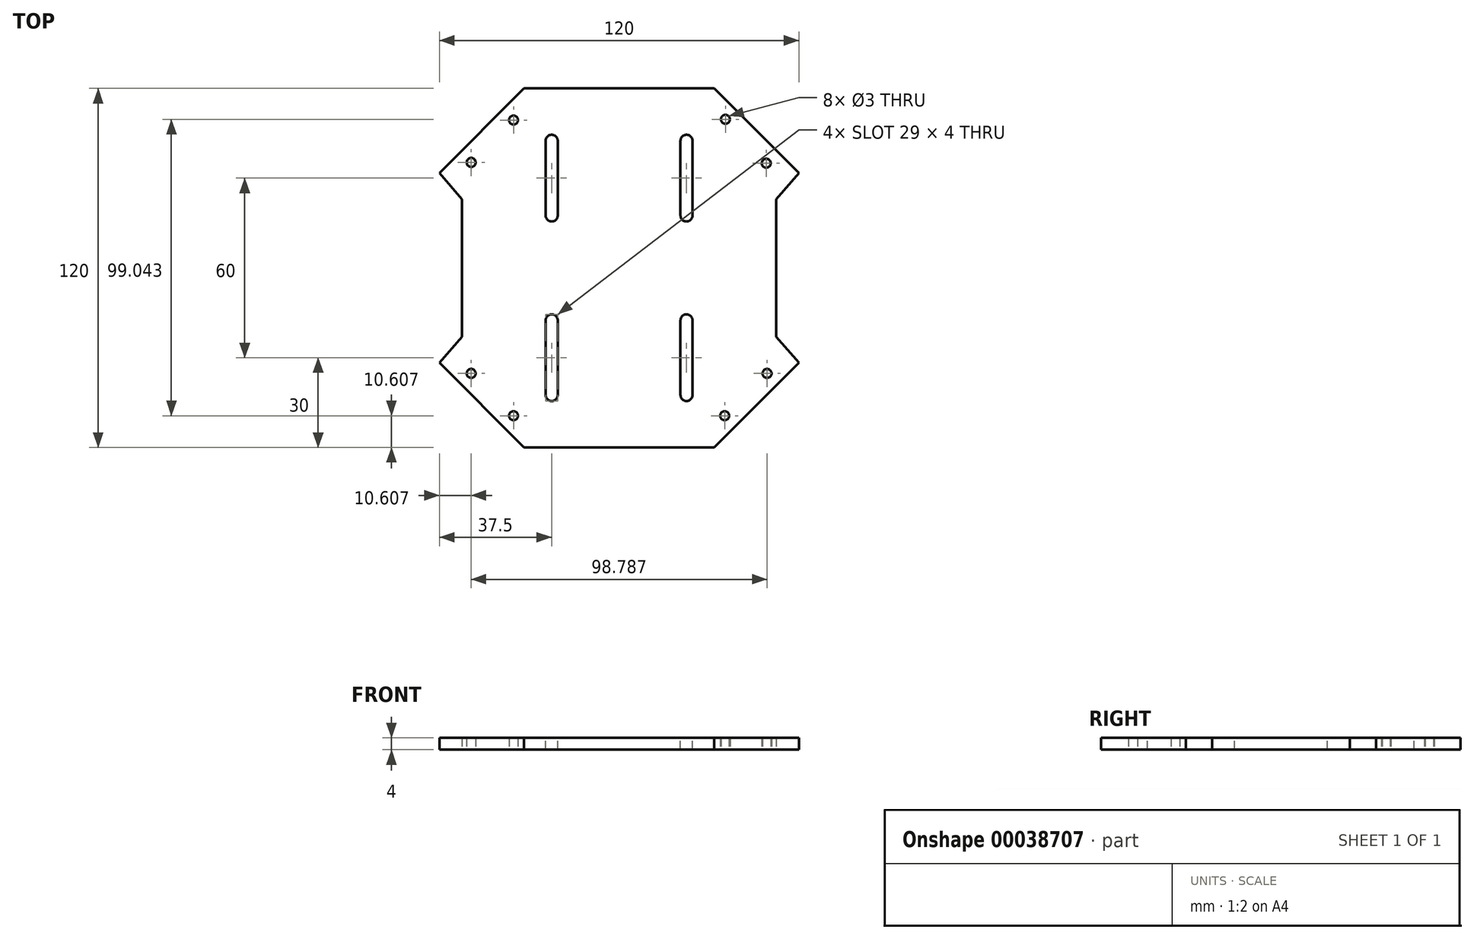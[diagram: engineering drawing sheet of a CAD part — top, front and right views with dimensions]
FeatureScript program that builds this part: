
annotation { "Feature Type Name" : "Feature", "Feature Type Description" : "" }
export const myFeature = defineFeature(function(context is Context, id is Id, definition is map)
    precondition{}
    {
        {
            var Q0;
            Q0=qCreatedBy(makeId("Top.planeOp"),FACE);
            var sketch = newSketch(context, id + "F0", { "sketchPlane" : qUnion([Q0])});
            skLineSegment(sketch, "E0.rect.bottom", {"start": v(32.5, 32.5) * mm, "end": v(-32.5, 32.5) * mm, "construction": true});
            skLineSegment(sketch, "E0.rect.top", {"start": v(32.5, -32.5) * mm, "end": v(-32.5, -32.5) * mm, "construction": true});
            skLineSegment(sketch, "E0.rect.left", {"start": v(32.5, 32.5) * mm, "end": v(32.5, -32.5) * mm, "construction": true});
            skLineSegment(sketch, "E0.rect.right", {"start": v(-32.5, 32.5) * mm, "end": v(-32.5, -32.5) * mm, "construction": true});
            skPoint(sketch, "E0.rect.middle", {"position": v(0, 0) * mm});
            skLineSegment(sketch, "E1", {"start": v(-32.5, -32.5) * mm, "end": v(32.5, 32.5) * mm, "construction": true});
            skLineSegment(sketch, "E2", {"start": v(-32.5, 32.5) * mm, "end": v(32.5, -32.5) * mm, "construction": true});
            skLineSegment(sketch, "E3.bottom", {"start": v(-137.78, 137.78) * mm, "end": v(137.78, 137.78) * mm, "construction": true});
            skLineSegment(sketch, "E3.top", {"start": v(-137.78, -137.78) * mm, "end": v(137.78, -137.78) * mm, "construction": true});
            skLineSegment(sketch, "E3.left", {"start": v(-137.78, 137.78) * mm, "end": v(-137.78, -137.78) * mm, "construction": true});
            skLineSegment(sketch, "E3.right", {"start": v(137.78, 137.78) * mm, "end": v(137.78, -137.78) * mm, "construction": true});
            skCircle(sketch, "E4", {"center": v(-137.78, 137.78) * mm, "radius": 101.5 * mm, "construction": true});
            skCircle(sketch, "E5", {"center": v(137.78, 137.78) * mm, "radius": 101.5 * mm, "construction": true});
            skCircle(sketch, "E6", {"center": v(137.78, -137.78) * mm, "radius": 101.5 * mm, "construction": true});
            skCircle(sketch, "E7", {"center": v(-137.78, -137.78) * mm, "radius": 101.5 * mm, "construction": true});
            skLineSegment(sketch, "E8.rect.bottom", {"start": v(-20.12, 56) * mm, "end": v(20.13, 56) * mm, "construction": true});
            skLineSegment(sketch, "E8.rect.top", {"start": v(-20.13, -56) * mm, "end": v(20.12, -56) * mm, "construction": true});
            skLineSegment(sketch, "E8.rect.left", {"start": v(-20.12, 56) * mm, "end": v(-20.13, -56) * mm, "construction": true});
            skLineSegment(sketch, "E8.rect.right", {"start": v(20.13, 56) * mm, "end": v(20.12, -56) * mm, "construction": true});
            skLineSegment(sketch, "E9.rect.bottom", {"start": v(-45.86, 45.86) * mm, "end": v(45.86, 45.86) * mm, "construction": true});
            skLineSegment(sketch, "E9.rect.top", {"start": v(-45.86, -45.86) * mm, "end": v(45.86, -45.86) * mm, "construction": true});
            skLineSegment(sketch, "E9.rect.left", {"start": v(-45.86, 45.86) * mm, "end": v(-45.86, -45.86) * mm, "construction": true});
            skLineSegment(sketch, "E9.rect.right", {"start": v(45.86, 45.86) * mm, "end": v(45.86, -45.86) * mm, "construction": true});
            skLineSegment(sketch, "E10", {"start": v(45.86, 45.86) * mm, "end": v(137.78, 137.78) * mm, "construction": true});
            skLineSegment(sketch, "E11", {"start": v(45.86, -45.86) * mm, "end": v(137.78, -137.78) * mm, "construction": true});
            skLineSegment(sketch, "E12", {"start": v(0, -137.78) * mm, "end": v(0, 137.78) * mm, "construction": true});
            skLineSegment(sketch, "E13", {"start": v(-137.78, -137.78) * mm, "end": v(-45.86, -45.86) * mm, "construction": true});
            skCircle(sketch, "E14", {"center": v(-137.78, 137.78) * mm, "radius": 14 * mm, "construction": true});
            skCircle(sketch, "E15", {"center": v(-137.78, 137.78) * mm, "radius": 20 * mm});
            skLineSegment(sketch, "E16", {"start": v(-60, 31.72) * mm, "end": v(-60, -31.72) * mm, "construction": true});
            skLineSegment(sketch, "E17", {"start": v(-60, -31.72) * mm, "end": v(-31.72, -60) * mm, "construction": true});
            skLineSegment(sketch, "E18", {"start": v(31.72, -60) * mm, "end": v(60, -31.72) * mm, "construction": true});
            skLineSegment(sketch, "E19", {"start": v(-31.72, -60) * mm, "end": v(31.72, -60) * mm, "construction": true});
            skLineSegment(sketch, "E20", {"start": v(60, -31.72) * mm, "end": v(60, 31.72) * mm, "construction": true});
            skLineSegment(sketch, "E21", {"start": v(31.72, 60) * mm, "end": v(60, 31.72) * mm, "construction": true});
            skLineSegment(sketch, "E22", {"start": v(-31.72, 60) * mm, "end": v(31.72, 60) * mm, "construction": true});
            skLineSegment(sketch, "E23", {"start": v(-151.92, 123.64) * mm, "end": v(-123.64, 151.92) * mm, "construction": true});
            skLineSegment(sketch, "E24", {"start": v(-52.5, 23) * mm, "end": v(-52.5, -23) * mm, "construction": true});
            skLineSegment(sketch, "E25", {"start": v(-52.5, 0) * mm, "end": v(-60, 0) * mm, "construction": true});
            skLineSegment(sketch, "E26", {"start": v(-60, 31.72) * mm, "end": v(-52.5, 23) * mm, "construction": true});
            skLineSegment(sketch, "E27", {"start": v(-60, -31.72) * mm, "end": v(-52.5, -23) * mm, "construction": true});
            skLineSegment(sketch, "E28", {"start": v(52.5, 23) * mm, "end": v(52.5, -23) * mm, "construction": true});
            skLineSegment(sketch, "E29", {"start": v(52.5, 0) * mm, "end": v(60, 0) * mm, "construction": true});
            skLineSegment(sketch, "E30", {"start": v(60, 31.72) * mm, "end": v(52.5, 23) * mm, "construction": true});
            skLineSegment(sketch, "E31", {"start": v(60, -31.72) * mm, "end": v(52.5, -23) * mm, "construction": true});
            skCircle(sketch, "E32", {"center": v(-137.78, -137.78) * mm, "radius": 20 * mm, "construction": true});
            skCircle(sketch, "E33", {"center": v(137.78, -137.78) * mm, "radius": 20 * mm, "construction": true});
            skCircle(sketch, "E34", {"center": v(137.78, 137.78) * mm, "radius": 20 * mm, "construction": true});
            skLineSegment(sketch, "E35", {"start": v(-151.92, -123.64) * mm, "end": v(-123.64, -151.92) * mm, "construction": true});
            skLineSegment(sketch, "E36", {"start": v(123.64, -151.92) * mm, "end": v(151.92, -123.64) * mm, "construction": true});
            skLineSegment(sketch, "E37", {"start": v(151, 122.77) * mm, "end": v(124.57, 152.8) * mm, "construction": true});
            skLineSegment(sketch, "E38", {"start": v(-60, 31.72) * mm, "end": v(-31.72, 60) * mm});
            skLineSegment(sketch, "E39", {"start": v(-45.86, 45.86) * mm, "end": v(-137.78, 137.78) * mm, "construction": true});
            skLineSegment(sketch, "E40", {"start": v(-112.33, 92.53) * mm, "end": v(-92.53, 112.33) * mm, "construction": true});
            skPoint(sketch, "E41", {"position": v(-102.43, 102.43) * mm});
            skLineSegment(sketch, "E42", {"start": v(-151.92, 123.64) * mm, "end": v(-112.33, 92.53) * mm});
            skLineSegment(sketch, "E43", {"start": v(-112.33, 92.53) * mm, "end": v(-60, 31.72) * mm});
            skLineSegment(sketch, "E44", {"start": v(-123.64, 151.92) * mm, "end": v(-92.53, 112.33) * mm});
            skLineSegment(sketch, "E45", {"start": v(-31.72, 60) * mm, "end": v(-92.53, 112.33) * mm});
            skLineSegment(sketch, "E46", {"start": v(-92.53, -112.33) * mm, "end": v(-112.33, -92.53) * mm, "construction": true});
            skPoint(sketch, "E47", {"position": v(-102.43, -102.43) * mm});
            skLineSegment(sketch, "E48", {"start": v(112.33, 92.53) * mm, "end": v(92.53, 112.33) * mm, "construction": true});
            skLineSegment(sketch, "E49", {"start": v(112.33, -92.53) * mm, "end": v(92.53, -112.33) * mm, "construction": true});
            skPoint(sketch, "E50", {"position": v(102.43, 102.43) * mm});
            skPoint(sketch, "E51", {"position": v(102.43, -102.43) * mm});
            skLineSegment(sketch, "E52", {"start": v(124.57, 152.8) * mm, "end": v(92.53, 112.33) * mm, "construction": true});
            skLineSegment(sketch, "E53", {"start": v(31.72, 60) * mm, "end": v(92.53, 112.33) * mm, "construction": true});
            skLineSegment(sketch, "E54", {"start": v(151, 122.77) * mm, "end": v(112.33, 92.53) * mm, "construction": true});
            skLineSegment(sketch, "E55", {"start": v(60, 31.72) * mm, "end": v(112.33, 92.53) * mm, "construction": true});
            skLineSegment(sketch, "E56", {"start": v(151.92, -123.64) * mm, "end": v(112.33, -92.53) * mm, "construction": true});
            skLineSegment(sketch, "E57", {"start": v(112.33, -92.53) * mm, "end": v(60, -31.72) * mm, "construction": true});
            skLineSegment(sketch, "E58", {"start": v(31.72, -60) * mm, "end": v(92.53, -112.33) * mm, "construction": true});
            skLineSegment(sketch, "E59", {"start": v(123.64, -151.92) * mm, "end": v(92.53, -112.33) * mm, "construction": true});
            skLineSegment(sketch, "E60", {"start": v(-123.64, -151.92) * mm, "end": v(-92.53, -112.33) * mm, "construction": true});
            skLineSegment(sketch, "E61", {"start": v(-31.72, -60) * mm, "end": v(-92.53, -112.33) * mm, "construction": true});
            skLineSegment(sketch, "E62", {"start": v(-60, -31.72) * mm, "end": v(-112.33, -92.53) * mm, "construction": true});
            skLineSegment(sketch, "E63", {"start": v(-151.92, -123.64) * mm, "end": v(-112.33, -92.53) * mm, "construction": true});
            skLineSegment(sketch, "E64", {"start": v(-53.46, 24.11) * mm, "end": v(-24.11, 53.46) * mm});
            skLineSegment(sketch, "E65", {"start": v(-24.11, 53.46) * mm, "end": v(-31.72, 60) * mm});
            skLineSegment(sketch, "E66", {"start": v(-53.46, 24.11) * mm, "end": v(-60, 31.72) * mm});
            skSolve(sketch);
        }
        {
            var Q0;
            Q0=qCreatedBy(makeId("Top.planeOp"),FACE);
            var sketch = newSketch(context, id + "F1", { "sketchPlane" : qUnion([Q0])});
            skLineSegment(sketch, "E67.0", {"start": v(-151.92, 123.64) * mm, "end": v(-112.33, 92.53) * mm});
            skLineSegment(sketch, "E68.0", {"start": v(-112.33, 92.53) * mm, "end": v(-60, 31.72) * mm});
            skLineSegment(sketch, "E68.1", {"start": v(-31.72, 60) * mm, "end": v(-92.53, 112.33) * mm});
            skLineSegment(sketch, "E68.2", {"start": v(-123.64, 151.92) * mm, "end": v(-92.53, 112.33) * mm});
            skCircle(sketch, "E68.3", {"center": v(-137.78, 137.78) * mm, "radius": 20 * mm});
            skLineSegment(sketch, "E68.4", {"start": v(-24.11, 53.46) * mm, "end": v(-31.72, 60) * mm});
            skLineSegment(sketch, "E68.5", {"start": v(-53.46, 24.11) * mm, "end": v(-60, 31.72) * mm});
            skLineSegment(sketch, "E68.6", {"start": v(-53.46, 24.11) * mm, "end": v(-24.11, 53.46) * mm});
            skSolve(sketch);
        }
        {
            var Q0;
            Q0=makeQuery(id+"FJeBJDLh8THmY7t_0.opExtrude","CAP_FACE",FACE,{"disambiguationData":[OSD([sQuery(id+"F1.wireOp",EDGE,"E67.0"),sQuery(id+"F1.wireOp",EDGE,"E68.0"),sQuery(id+"F1.wireOp",EDGE,"E68.1"),sQuery(id+"F1.wireOp",EDGE,"E68.2"),sQuery(id+"F1.wireOp",EDGE,"E68.3"),sQuery(id+"F1.wireOp",EDGE,"E68.4"),sQuery(id+"F1.wireOp",EDGE,"E68.5"),sQuery(id+"F1.wireOp",EDGE,"E68.6")])],"isStart":false});
            var sketch = newSketch(context, id + "F2", { "sketchPlane" : qUnion([Q0])});
            skCircle(sketch, "E69.0", {"center": v(-137.78, -137.78) * mm, "radius": 20 * mm});
            skLineSegment(sketch, "E70.0", {"start": v(-60, -31.72) * mm, "end": v(-31.72, -60) * mm});
            skLineSegment(sketch, "E71.0", {"start": v(-24.11, -53.46) * mm, "end": v(-49.65, -27.92) * mm});
            skLineSegment(sketch, "E71.1", {"start": v(-92.53, -112.33) * mm, "end": v(-24.11, -53.46) * mm});
            skLineSegment(sketch, "E71.2", {"start": v(-120.9, -148.43) * mm, "end": v(-92.53, -112.33) * mm});
            skLineSegment(sketch, "E72.0", {"start": v(-109.55, -95.43) * mm, "end": v(-145.9, -124) * mm});
            skLineSegment(sketch, "E72.1", {"start": v(-124, -145.9) * mm, "end": v(-95.43, -109.55) * mm});
            skLineSegment(sketch, "E72.2", {"start": v(-95.43, -109.55) * mm, "end": v(-34.55, -57.16) * mm});
            skArc(sketch, "E72.3", {"start": v(-145.9, -124) * mm, "mid": v(-149.1, -149.1) * mm, "end": v(-124, -145.9) * mm});
            skLineSegment(sketch, "E72.5", {"start": v(-57.16, -34.55) * mm, "end": v(-109.55, -95.43) * mm});
            skLineSegment(sketch, "E73.0", {"start": v(-45.86, -45.86) * mm, "end": v(-123.64, -123.64) * mm, "construction": true});
            skLineSegment(sketch, "E74.0", {"start": v(-46.92, -44.8) * mm, "end": v(-124.74, -122.62) * mm});
            skLineSegment(sketch, "E75.0", {"start": v(-44.8, -46.92) * mm, "end": v(-122.62, -124.74) * mm});
            skSolve(sketch);
        }
        {
            var Q0;
            Q0=makeQuery(id+"FfZ2kWWbx0hkoDQ_1.boolean.opBoolean","MERGE",FACE,{"derivedFrom":[makeQuery(id+"FJeBJDLh8THmY7t_0.opExtrude","CAP_FACE",FACE,{"disambiguationData":[OSD([sQuery(id+"F1.wireOp",EDGE,"E67.0"),sQuery(id+"F1.wireOp",EDGE,"E68.0"),sQuery(id+"F1.wireOp",EDGE,"E68.1"),sQuery(id+"F1.wireOp",EDGE,"E68.2"),sQuery(id+"F1.wireOp",EDGE,"E68.3"),sQuery(id+"F1.wireOp",EDGE,"E68.4"),sQuery(id+"F1.wireOp",EDGE,"E68.5"),sQuery(id+"F1.wireOp",EDGE,"E68.6")])],"isStart":false}),makeQuery(id+"FfZ2kWWbx0hkoDQ_1.opExtrude","CAP_FACE",FACE,{"disambiguationData":[OSD([sQuery(id+"F2.wireOp",EDGE,"E72.0"),sQuery(id+"F2.wireOp",EDGE,"E72.1"),sQuery(id+"F2.wireOp",EDGE,"E72.2"),sQuery(id+"F2.wireOp",EDGE,"E72.5"),sQuery(id+"F2.wireOp",EDGE,"E74.0"),sQuery(id+"F2.wireOp",EDGE,"E75.0"),sQuery(id+"FiQxRTnNKV71TQx_1.wireOp",EDGE,"38970236-bfd6-4454-96b1-5af9a77133ed.0"),sQuery(id+"FiQxRTnNKV71TQx_1.wireOp",EDGE,"38970236-bfd6-4454-96b1-5af9a77133ed.1"),sQuery(id+"FiQxRTnNKV71TQx_1.wireOp",EDGE,"38970236-bfd6-4454-96b1-5af9a77133ed.2"),sQuery(id+"FiQxRTnNKV71TQx_1.wireOp",EDGE,"38970236-bfd6-4454-96b1-5af9a77133ed.3"),sQuery(id+"FiQxRTnNKV71TQx_1.wireOp",EDGE,"38970236-bfd6-4454-96b1-5af9a77133ed.4"),sQuery(id+"FiQxRTnNKV71TQx_1.wireOp",EDGE,"38970236-bfd6-4454-96b1-5af9a77133ed.5"),sQuery(id+"FiQxRTnNKV71TQx_1.wireOp",EDGE,"38970236-bfd6-4454-96b1-5af9a77133ed.6"),sQuery(id+"FiQxRTnNKV71TQx_1.wireOp",EDGE,"38970236-bfd6-4454-96b1-5af9a77133ed.7"),sQuery(id+"FiQxRTnNKV71TQx_1.wireOp",EDGE,"38970236-bfd6-4454-96b1-5af9a77133ed.11"),sQuery(id+"FiQxRTnNKV71TQx_1.wireOp",EDGE,"84821af2-2a79-4291-835d-9572d2859dc5.1"),sQuery(id+"FiQxRTnNKV71TQx_1.wireOp",EDGE,"84821af2-2a79-4291-835d-9572d2859dc5.2"),sQuery(id+"FiQxRTnNKV71TQx_1.wireOp",EDGE,"84821af2-2a79-4291-835d-9572d2859dc5.3"),sQuery(id+"FiQxRTnNKV71TQx_1.wireOp",EDGE,"84821af2-2a79-4291-835d-9572d2859dc5.4"),sQuery(id+"FiQxRTnNKV71TQx_1.wireOp",EDGE,"84821af2-2a79-4291-835d-9572d2859dc5.5"),sQuery(id+"FiQxRTnNKV71TQx_1.wireOp",EDGE,"84821af2-2a79-4291-835d-9572d2859dc5.6"),sQuery(id+"FiQxRTnNKV71TQx_1.wireOp",EDGE,"84821af2-2a79-4291-835d-9572d2859dc5.7"),sQuery(id+"FiQxRTnNKV71TQx_1.wireOp",EDGE,"84821af2-2a79-4291-835d-9572d2859dc5.8"),sQuery(id+"FiQxRTnNKV71TQx_1.wireOp",EDGE,"84821af2-2a79-4291-835d-9572d2859dc5.11"),sQuery(id+"FiQxRTnNKV71TQx_1.wireOp",EDGE,"8611adc8-e619-4c53-af6e-c2d4046b9e3c0.MirrorCS"),sQuery(id+"FiQxRTnNKV71TQx_1.wireOp",EDGE,"d0435597-b384-4ab9-9637-6f22e2db63830.MirrorCS"),sQuery(id+"FiQxRTnNKV71TQx_1.wireOp",EDGE,"db108342-3424-454d-b83c-aa2f3f1c2cb20.MirrorCS"),sQuery(id+"FiQxRTnNKV71TQx_1.wireOp",EDGE,"8967fe85-72d8-4dfa-971c-bef20ae89da20.MirrorCS"),sQuery(id+"FiQxRTnNKV71TQx_1.wireOp",EDGE,"f7285943-b11e-44b1-814a-c0c81710d16c0.MirrorCS"),sQuery(id+"FiQxRTnNKV71TQx_1.wireOp",EDGE,"30e0d23f-14ae-41a2-b20f-fbc5a62c98db0.MirrorCS"),sQuery(id+"FiQxRTnNKV71TQx_1.wireOp",EDGE,"1f170661-e214-4223-ba55-c6e99d467d940.MirrorCS"),sQuery(id+"FiQxRTnNKV71TQx_1.wireOp",EDGE,"0d6bcc0d-2ce1-4a65-832b-dffd11caf7e80.MirrorCS"),sQuery(id+"FiQxRTnNKV71TQx_1.wireOp",EDGE,"7abc0380-5524-41c7-a0ce-68a4796d5a7b0.MirrorCS"),sQuery(id+"FiQxRTnNKV71TQx_1.wireOp",EDGE,"19e96206-981b-43be-ba05-1c10bb68f1450.MirrorCS"),sQuery(id+"FiQxRTnNKV71TQx_1.wireOp",EDGE,"2ea1ab67-ca09-4ed3-820a-d74567cfc47a0.MirrorCS"),sQuery(id+"FiQxRTnNKV71TQx_1.wireOp",EDGE,"91afe6bc-90b4-4b5e-82f6-75096f2b2aa40.MirrorCS"),sQuery(id+"FiQxRTnNKV71TQx_1.wireOp",EDGE,"e83ae27f-a570-4dcf-a388-984b5eeb59020.MirrorCS"),sQuery(id+"FiQxRTnNKV71TQx_1.wireOp",EDGE,"90c546e3-c060-4be6-aa96-ffa96f1bf26c0.MirrorCS"),sQuery(id+"FiQxRTnNKV71TQx_1.wireOp",EDGE,"99bcaea7-dbcd-4b30-a0d6-bc1ef52a4ca00.MirrorCS"),sQuery(id+"FiQxRTnNKV71TQx_1.wireOp",EDGE,"c8000fa1-2a0c-4d24-8a33-407feac34fb10.MirrorCS"),sQuery(id+"FiQxRTnNKV71TQx_1.wireOp",EDGE,"3c656657-db58-4b72-afe2-c262a7839c5d0.MirrorCS"),sQuery(id+"FiQxRTnNKV71TQx_1.wireOp",EDGE,"813f3043-2374-4368-9225-d27bba9bf23f0.MirrorCS"),sQuery(id+"FiQxRTnNKV71TQx_1.wireOp",EDGE,"YwUhEMed-aB1d-ipUQ-UnQH-Itm6UoLuJCMO"),sQuery(id+"FiQxRTnNKV71TQx_1.wireOp",EDGE,"h0J1Apl3-0yBk-VO02-KO2W-2kVpn1Ds907W"),sQuery(id+"FiQxRTnNKV71TQx_1.wireOp",EDGE,"vqShVz5m-KmEU-cyHf-AfiJ-yMXPyKyrkMLc"),sQuery(id+"FiQxRTnNKV71TQx_1.wireOp",EDGE,"wBHHw6Ij-qgAp-Wx4X-vHHM-6AXWrW058tig"),sQuery(id+"FiQxRTnNKV71TQx_1.wireOp",EDGE,"UQsRDA6M-BFFb-5RWh-NpgG-BJ7fZ36mSHP9"),sQuery(id+"FiQxRTnNKV71TQx_1.wireOp",EDGE,"gtlBCoMz-qEui-tsZH-9I7z-61eOqyYzUrIE"),sQuery(id+"FiQxRTnNKV71TQx_1.wireOp",EDGE,"5JgQ3pHy-WNFa-i7Q0-qU2A-RRM7FCAXBTSd"),sQuery(id+"FiQxRTnNKV71TQx_1.wireOp",EDGE,"w7owdK0z-TjIJ-COOg-YfHl-q6q5tVCwM537")])],"isStart":true})]});
            var sketch = newSketch(context, id + "F3", { "sketchPlane" : qUnion([Q0])});
            skLineSegment(sketch, "E76", {"start": v(-151.92, -151.92) * mm, "end": v(-38.79, -38.79) * mm, "construction": true});
            skArc(sketch, "E77.0", {"start": v(-120.7, -148.18) * mm, "mid": v(-151.92, -151.92) * mm, "end": v(-148.18, -120.7) * mm, "construction": true});
            skLineSegment(sketch, "E78", {"start": v(-137.78, -129.78) * mm, "end": v(-137.78, -145.78) * mm, "construction": true});
            skPoint(sketch, "E78.startSnap0", {"position": v(-137.78, -131.9) * mm});
            skLineSegment(sketch, "E79", {"start": v(-147.28, -137.78) * mm, "end": v(-128.28, -137.78) * mm, "construction": true});
            skPoint(sketch, "E80", {"position": v(-137.78, -129.78) * mm});
            skPoint(sketch, "E81", {"position": v(-128.28, -137.78) * mm});
            skPoint(sketch, "E82", {"position": v(-137.78, -145.78) * mm});
            skPoint(sketch, "E83", {"position": v(-147.28, -137.78) * mm});
            skLineSegment(sketch, "E84", {"start": v(-31.72, -60) * mm, "end": v(-24.64, -52.93) * mm, "construction": true});
            skLineSegment(sketch, "E85", {"start": v(-45.86, -45.86) * mm, "end": v(-38.79, -38.79) * mm, "construction": true});
            skPoint(sketch, "E86", {"position": v(-42.32, -42.32) * mm});
            skLineSegment(sketch, "E87", {"start": v(-49.4, -35.25) * mm, "end": v(-35.25, -49.4) * mm, "construction": true});
            skCircle(sketch, "E88", {"center": v(-137.78, -137.78) * mm, "radius": 4 * mm});
            skSolve(sketch);
        }
        {
            var Q0;
            Q0=qCreatedBy(makeId("Top.planeOp"),FACE);
            var sketch = newSketch(context, id + "F4", { "sketchPlane" : qUnion([Q0])});
            skLineSegment(sketch, "E89.0", {"start": v(-31.72, 60) * mm, "end": v(31.72, 60) * mm});
            skLineSegment(sketch, "E89.1", {"start": v(-60, 31.72) * mm, "end": v(-31.72, 60) * mm});
            skLineSegment(sketch, "E89.2", {"start": v(-60, 31.72) * mm, "end": v(-52.5, 23) * mm});
            skLineSegment(sketch, "E89.3", {"start": v(-52.5, 23) * mm, "end": v(-52.5, -23) * mm});
            skLineSegment(sketch, "E89.4", {"start": v(-60, -31.72) * mm, "end": v(-52.5, -23) * mm});
            skLineSegment(sketch, "E89.5", {"start": v(-60, -31.72) * mm, "end": v(-31.72, -60) * mm});
            skLineSegment(sketch, "E89.6", {"start": v(-31.72, -60) * mm, "end": v(31.72, -60) * mm});
            skLineSegment(sketch, "E89.7", {"start": v(31.72, -60) * mm, "end": v(60, -31.72) * mm});
            skLineSegment(sketch, "E89.8", {"start": v(31.72, 60) * mm, "end": v(60, 31.72) * mm});
            skLineSegment(sketch, "E89.9", {"start": v(60, 31.72) * mm, "end": v(52.5, 23) * mm});
            skLineSegment(sketch, "E89.10", {"start": v(60, -31.72) * mm, "end": v(52.5, -23) * mm});
            skLineSegment(sketch, "E89.11", {"start": v(52.5, 23) * mm, "end": v(52.5, -23) * mm});
            skLineSegment(sketch, "E89.12", {"start": v(-49.4, 35.25) * mm, "end": v(-35.25, 49.4) * mm});
            skPoint(sketch, "E89.13", {"position": v(-35.25, 49.4) * mm});
            skPoint(sketch, "E89.14", {"position": v(-49.4, 35.25) * mm});
            skLineSegment(sketch, "E89.15", {"start": v(-53.46, 24.11) * mm, "end": v(-60, 31.72) * mm});
            skLineSegment(sketch, "E90", {"start": v(-42.32, 42.32) * mm, "end": v(-45.86, 45.86) * mm});
            skLineSegment(sketch, "E91", {"start": v(45.86, 45.86) * mm, "end": v(42.32, 42.32) * mm});
            skLineSegment(sketch, "E92", {"start": v(35.52, 49.65) * mm, "end": v(49.13, 35) * mm});
            skLineSegment(sketch, "E93", {"start": v(45.86, -45.86) * mm, "end": v(42.32, -42.32) * mm});
            skLineSegment(sketch, "E94", {"start": v(-45.86, -45.86) * mm, "end": v(-42.32, -42.32) * mm});
            skLineSegment(sketch, "E95", {"start": v(-49.4, -35.25) * mm, "end": v(-35.25, -49.4) * mm});
            skLineSegment(sketch, "E96", {"start": v(35.25, -49.4) * mm, "end": v(49.4, -35.25) * mm});
            skSolve(sketch);
        }
        {
            var Q0;
            {var subQ1=sQuery(id+"F4.wireOp",EDGE,"E89.0");Q0=makeQuery(id+"F4.imprint","IMPRINT",FACE,{"disambiguationData":[TD([[makeQuery(id+"F4.imprint","IMPRINT",EDGE,{"derivedFrom":subQ1}),-1.0]])]});}
            extrude(context, id + "F5", {"entities" : qUnion([Q0]), "depth" : 4 * mm});
        }
        {
            var Q0;
            Q0=makeQuery(id+"F5.opExtrude","CAP_FACE",FACE,{"disambiguationData":[OSD([sQuery(id+"F4.wireOp",EDGE,"E89.0"),sQuery(id+"F4.wireOp",EDGE,"E89.2"),sQuery(id+"F4.wireOp",EDGE,"E89.3"),sQuery(id+"F4.wireOp",EDGE,"E89.4"),sQuery(id+"F4.wireOp",EDGE,"E89.5"),sQuery(id+"F4.wireOp",EDGE,"E89.6"),sQuery(id+"F4.wireOp",EDGE,"E89.7"),sQuery(id+"F4.wireOp",EDGE,"E89.8"),sQuery(id+"F4.wireOp",EDGE,"E89.9"),sQuery(id+"F4.wireOp",EDGE,"E89.10"),sQuery(id+"F4.wireOp",EDGE,"E89.11"),sQuery(id+"F4.wireOp",EDGE,"E89.15"),sQuery(id+"F4.wireOp",EDGE,"E89.1")])],"isStart":false});
            var sketch = newSketch(context, id + "F6", { "sketchPlane" : qUnion([Q0])});
            skLineSegment(sketch, "E97", {"start": v(0, -60) * mm, "end": v(0, 60) * mm, "construction": true});
            skLineSegment(sketch, "E98", {"start": v(-52.5, 0) * mm, "end": v(52.5, 0) * mm, "construction": true});
            skPoint(sketch, "E99", {"position": v(0, 0) * mm});
            skPoint(sketch, "E100", {"position": v(-40.75, 0) * mm});
            skPoint(sketch, "E101", {"position": v(40.75, 0) * mm});
            skLineSegment(sketch, "E102", {"start": v(-40.75, 0) * mm, "end": v(40.75, 0) * mm});
            skLineSegment(sketch, "E103", {"start": v(40.75, 8) * mm, "end": v(40.75, -8) * mm});
            skSolve(sketch);
        }
        {
            var Q0;
            Q0=sQuery(id+"F4.wireOp",VERTEX,"E89.14");
            var Q1;
            Q1=sQuery(id+"F4.wireOp",VERTEX,"E89.13");
            var Q2;
            Q2=sQuery(id+"F4.wireOp",VERTEX,"E92.start");
            var Q3;
            Q3=sQuery(id+"F4.wireOp",VERTEX,"E92.end");
            var Q4;
            Q4=sQuery(id+"F4.wireOp",VERTEX,"E96.end");
            var Q5;
            Q5=sQuery(id+"F4.wireOp",VERTEX,"E96.start");
            var Q6;
            Q6=sQuery(id+"F4.wireOp",VERTEX,"E95.end");
            var Q7;
            Q7=sQuery(id+"F4.wireOp",VERTEX,"E95.start");
            var Q8;
            Q8=makeQuery(id+"F5.opExtrude","SWEPT_BODY",BODY,{"disambiguationData":[OSD([sQuery(id+"F4.wireOp",EDGE,"E89.0"),sQuery(id+"F4.wireOp",EDGE,"E89.2"),sQuery(id+"F4.wireOp",EDGE,"E89.3"),sQuery(id+"F4.wireOp",EDGE,"E89.4"),sQuery(id+"F4.wireOp",EDGE,"E89.5"),sQuery(id+"F4.wireOp",EDGE,"E89.6"),sQuery(id+"F4.wireOp",EDGE,"E89.7"),sQuery(id+"F4.wireOp",EDGE,"E89.8"),sQuery(id+"F4.wireOp",EDGE,"E89.9"),sQuery(id+"F4.wireOp",EDGE,"E89.10"),sQuery(id+"F4.wireOp",EDGE,"E89.11"),sQuery(id+"F4.wireOp",EDGE,"E89.15"),sQuery(id+"F4.wireOp",EDGE,"E89.1")])]});
            hole(context, id + "F7", {"style" : HoleStyle.SIMPLE, "holeDiameter" : 3 * mm, "endStyle" : HoleEndStyle.THROUGH, "oppositeDirection" : true, "locations" : qUnion([Q0, Q1, Q2, Q3, Q4, Q5, Q6, Q7]), "scope" : qUnion([Q8])});
        }
        {
            var Q0;
            Q0=makeQuery(id+"F5.opExtrude","CAP_FACE",FACE,{"disambiguationData":[OSD([sQuery(id+"F4.wireOp",EDGE,"E89.0"),sQuery(id+"F4.wireOp",EDGE,"E89.2"),sQuery(id+"F4.wireOp",EDGE,"E89.3"),sQuery(id+"F4.wireOp",EDGE,"E89.4"),sQuery(id+"F4.wireOp",EDGE,"E89.5"),sQuery(id+"F4.wireOp",EDGE,"E89.6"),sQuery(id+"F4.wireOp",EDGE,"E89.7"),sQuery(id+"F4.wireOp",EDGE,"E89.8"),sQuery(id+"F4.wireOp",EDGE,"E89.9"),sQuery(id+"F4.wireOp",EDGE,"E89.10"),sQuery(id+"F4.wireOp",EDGE,"E89.11"),sQuery(id+"F4.wireOp",EDGE,"E89.15"),sQuery(id+"F4.wireOp",EDGE,"E89.1")])],"isStart":false});
            var sketch = newSketch(context, id + "F8", { "sketchPlane" : qUnion([Q0])});
            skLineSegment(sketch, "E104", {"start": v(0, 60) * mm, "end": v(0, -60) * mm, "construction": true});
            skLineSegment(sketch, "E105", {"start": v(-22.5, 30) * mm, "end": v(22.5, 30) * mm, "construction": true});
            skLineSegment(sketch, "E106", {"start": v(-22.5, -30) * mm, "end": v(22.5, -30) * mm, "construction": true});
            skPoint(sketch, "E107", {"position": v(0, 30) * mm});
            skPoint(sketch, "E108", {"position": v(0, -30) * mm});
            skLineSegment(sketch, "E109", {"start": v(-22.5, 42.5) * mm, "end": v(-22.5, 17.5) * mm, "construction": true});
            skLineSegment(sketch, "E110", {"start": v(-22.5, -17.5) * mm, "end": v(-22.5, -42.5) * mm, "construction": true});
            skLineSegment(sketch, "E111", {"start": v(22.5, 42.5) * mm, "end": v(22.5, 17.5) * mm, "construction": true});
            skLineSegment(sketch, "E112", {"start": v(22.5, -42.5) * mm, "end": v(22.5, -17.5) * mm, "construction": true});
            skArc(sketch, "E113.0.startCap", {"start": v(-24.5, 42.5) * mm, "mid": v(-22.5, 44.5) * mm, "end": v(-20.5, 42.5) * mm});
            skArc(sketch, "E113.0.endCap", {"start": v(-20.5, 17.5) * mm, "mid": v(-22.5, 15.5) * mm, "end": v(-24.5, 17.5) * mm});
            skLineSegment(sketch, "E113.0.left", {"start": v(-20.5, 42.5) * mm, "end": v(-20.5, 17.5) * mm});
            skLineSegment(sketch, "E113.0.right", {"start": v(-24.5, 42.5) * mm, "end": v(-24.5, 17.5) * mm});
            skArc(sketch, "E113.1.startCap", {"start": v(20.5, 42.5) * mm, "mid": v(22.5, 44.5) * mm, "end": v(24.5, 42.5) * mm});
            skArc(sketch, "E113.1.endCap", {"start": v(24.5, 17.5) * mm, "mid": v(22.5, 15.5) * mm, "end": v(20.5, 17.5) * mm});
            skLineSegment(sketch, "E113.1.left", {"start": v(24.5, 42.5) * mm, "end": v(24.5, 17.5) * mm});
            skLineSegment(sketch, "E113.1.right", {"start": v(20.5, 42.5) * mm, "end": v(20.5, 17.5) * mm});
            skArc(sketch, "E113.2.startCap", {"start": v(24.5, -42.5) * mm, "mid": v(22.5, -44.5) * mm, "end": v(20.5, -42.5) * mm});
            skArc(sketch, "E113.2.endCap", {"start": v(20.5, -17.5) * mm, "mid": v(22.5, -15.5) * mm, "end": v(24.5, -17.5) * mm});
            skLineSegment(sketch, "E113.2.left", {"start": v(20.5, -42.5) * mm, "end": v(20.5, -17.5) * mm});
            skLineSegment(sketch, "E113.2.right", {"start": v(24.5, -42.5) * mm, "end": v(24.5, -17.5) * mm});
            skArc(sketch, "E113.3.startCap", {"start": v(-24.5, -17.5) * mm, "mid": v(-22.5, -15.5) * mm, "end": v(-20.5, -17.5) * mm});
            skArc(sketch, "E113.3.endCap", {"start": v(-20.5, -42.5) * mm, "mid": v(-22.5, -44.5) * mm, "end": v(-24.5, -42.5) * mm});
            skLineSegment(sketch, "E113.3.left", {"start": v(-20.5, -17.5) * mm, "end": v(-20.5, -42.5) * mm});
            skLineSegment(sketch, "E113.3.right", {"start": v(-24.5, -17.5) * mm, "end": v(-24.5, -42.5) * mm});
            skSolve(sketch);
        }
        {
            var Q0;
            Q0 = qSketchRegion(id + "F8", true);
            var Q1;
            Q1=makeQuery(id+"F0.imprint","IMPRINT",FACE,{"disambiguationData":[TD([[makeQuery(id+"F0.imprint","IMPRINT",EDGE,{"derivedFrom":sQuery(id+"F0.wireOp",EDGE,"E38")}),1.0]])]});
            extrude(context, id + "F9", {"entities" : qUnion([Q0, Q1]), "operationType" : NewBodyOperationType.REMOVE, "endBound" : BoundingType.THROUGH_ALL, "oppositeDirection" : true, "depth" : 25 * mm});
        }
    });
